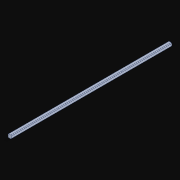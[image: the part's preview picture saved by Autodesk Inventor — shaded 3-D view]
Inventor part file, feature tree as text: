
AUTODESK INVENTOR PART (.ipt)
format: ipt  version: 2021 (Build 250183000, 183)  size: 156,160 bytes
history: native  units: in
note: dims shown in document units (in); Inventor stores cm internally (conversion verified against a paired STEP export)
features: other x50, extrude x2, sketch x2, thicken_offset x1
ambient origin geometry x8: Origin, YZ Plane, XZ Plane, XY Plane, X Axis, Y Axis, Z Axis, Center Point
bodies: Solid1 (feature_tree)
feature tree (55):
  other  "Table"
  other  "Shaft HS 0.5 in"
  other  "Shaft HS 1.0 in"
  other  "Shaft HS 1.5 in"
  other  "Shaft HS 2.0 in"
  other  "Shaft HS 2.5 in"
  other  "Shaft HS 3.0 in"
  other  "Shaft HS 3.5 in"
  other  "Shaft HS 4.0 in"
  other  "Shaft HS 4.5 in"
  other  "Shaft HS 5.0 in"
  other  "Shaft HS 5.5 in"
  other  "Shaft HS 6.0 in"
  other  "Shaft HS 6.5 in"
  other  "Shaft HS 7.0 in"
  other  "Shaft HS 7.5 in"
  other  "Shaft HS 8.0 in"
  other  "Shaft HS 8.5 in"
  other  "Shaft HS 9.0 in"
  other  "Shaft HS 9.5 in"
  other  "Shaft HS 10.0 in"
  other  "Shaft HS 10.5 in"
  other  "Shaft HS 11.0 in"
  other  "Shaft HS 11.5 in"
  other  "Shaft HS 12.0 in"
  other  "Shaft HS 12.5 in"
  other  "Shaft HS 13.0 in"
  other  "Shaft HS 13.5 in"
  other  "Shaft HS 14.0 in"
  other  "Shaft HS 14.5 in"
  other  "Shaft HS 15.0 in"
  other  "Shaft HS 15.5 in"
  other  "Shaft HS 16.0 in"
  other  "Shaft HS 16.5 in"
  other  "Shaft HS 17.0 in"
  other  "Shaft HS 17.5 in"
  other  "Shaft HS 18.0 in"
  other  "Shaft HS 18.5 in"
  other  "Shaft HS 19.0 in"
  other  "Shaft HS 19.5 in"
  other  "Shaft HS 20.0 in"
  other  "Shaft HS 20.5 in"
  other  "Shaft HS 21.0 in"
  other  "Shaft HS 21.5 in"
  other  "Shaft HS 22.0 in"
  other  "Shaft HS 22.5 in"
  other  "Shaft HS 23.0 in"
  other  "Shaft HS 23.5 in"
  other  "Shaft HS 24.0 in"
  extrude  "Extrusion1"  Depth=12.1875in
  thicken_offset  "Thicken1"
  extrude  "Extrusion2"  Depth=12.125in
  sketch  "Sketch2"  dims[d0=0.0625in d1=0.0in d2=12.1875in]
  sketch  "Sketch3"  dims[d3=12.125in d4=12.125in d5=0.0in]
  other  "Cut-Revolve3"
